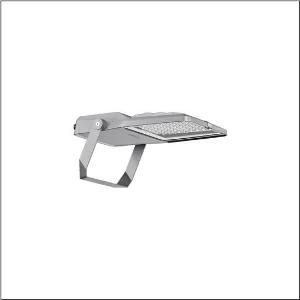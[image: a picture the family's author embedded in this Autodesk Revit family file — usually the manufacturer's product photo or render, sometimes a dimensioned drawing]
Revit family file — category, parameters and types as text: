
# Revit family: floodlight_fl_21_iq_mini___pl64_5xa7771d4e1a_9fb1
name_source: partatom
category: Lighting Fixtures
units: mm (PartAtom-declared; Revit-internal decimal feet)

## family parameters
Cut with Voids When Loaded = No
Host = Face
Light Source = No
Part Type = Normal
Room Calculation Point = No
Round Connector Dimension = Use Diameter
Shared = No

## types (1)
- --- (1 x LED, 17970 lm, 143 W, 4000K)
    Apparent Load = 143 VA
    CIE Flux Codes = 28 80 98 100 100
    Color Rendering = 70
    Color Temperature = 4000K
    Default Elevation = 1800 mm
    Description = Floodlight FL 21 iQ mini, floodlight, primary light control with lens, of PMMA, primary optical cover: protective disc, of toughened safety glass, transparent, light distribution: PL64, light emission: direct distribution, installation type: surface-mounted, LED, High Power LED, rated luminous flux: 17.970lm, luminous efficacy: 126lm/W, light colour: 740, colour temperature: 4000K, control: Auto-Match, Temp-Guard, Lumen-Switch, Night-Set, Smart-Wire, Light-Fading, Desk-Remote (wireless, voltage-free reading and setting of iQ features in the workshop via application-optimized NFC function/RFID function), optimised constant luminous flux control (CLO 2.0), with terminal, 6-pole, mains connection: 220..240V, AC, 50/60Hz, start of lifetime: 143W, end of service life: 152W, reduction: 61W, luminaire housing, of diecast aluminium, powder-coated, Siteco® metallic grey (DB 702S), corrosivity category C5 mid according to DIN EN ISO 12944, sealing non-destructively replaceable, mounting bracket, of steel, galvanised, powder-coated, Siteco® metallic grey (DB 702S), protection rating (complete): IP66, insulation class (complete): insulation class II (safety insulation), certification: CE, ENEC, VDE, protection symbol: D, impact resistance: IK08, permissible operating ambient temperature: -40..+40°C, permissible operating ambient temperature for outdoor applications: -40..+50°C, standard: DIN EN 12944, LABS conformity tested according to VDMA 24364:2018-05, packaging unit: 1 piece

Light Distribution: PL64
    Height = 70 mm
    Lamp = 1 x LED
    Lamp Light Flux = 17970 lm
    Lamp Power = 143 W
    Lamp count = 1
    Length = 485 mm
    Luminous efficacy = 126 lm/W
    Manufacturer = Siteco
    ModVariant = No
    Model = 5XA7771D4E1A
    Number of Poles = 1
    OnlyDefault = Yes
    Power Factor = 1
    Product Name = Floodlight FL 21 iQ mini | PL64
    Product group = floodlight | pylon annexe
    ProductGroupID = 6200
    Protection Class = Protection class II
    Protection Degree = IP 66
    RLX_Detail_Level = 1
    RLX_Emergency_Light_Flux = 0 lm
    RLX_Emergency_Type = 0
    RLX_Emergency_Type_DB = No
    RlxData = <blob elided: 96501 chars, md5=6a484d40>
    Socket = socket
    Standby Power = 0 W
    System Light Flux = 17970 lm
    System Power = 143 W
    Type Comments = factory setting: luminous flux: 100 % | dim-lin: 254 | 730 mA
    Type Image = l_1006845.jpg
    URL = http://relux.com
    VarID = @adj_116181
    Voltage = 0 V
    Weight = 0.00 kg
    Width = 337 mm

## geometry (parser evidence)
native form markers: Blend x4, Sweep x12
no freeform markers — native parametric forms only
